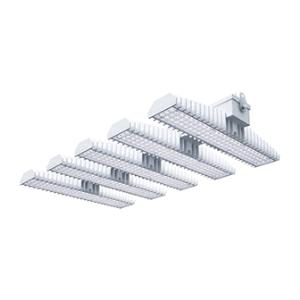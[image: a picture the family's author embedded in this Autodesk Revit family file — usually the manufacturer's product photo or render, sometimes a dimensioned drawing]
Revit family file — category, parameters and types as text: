
# Revit family: 3f_filippi_-_3f_lem_ho_ampio_3f_filippi_-_58976_a0811_-_3f_lem_5_ho_led_350_dali_cr_ampio___vt_9d90
name_source: partatom
category: Lighting Fixtures
units: mm (PartAtom-declared; Revit-internal decimal feet)

## family parameters
Cut with Voids When Loaded = No
Host = Face
Light Source = No
Part Type = Normal
Room Calculation Point = No
Round Connector Dimension = Use Diameter
Shared = No

## types (1)
- 3F Filippi - 3F LEM HO Ampio (1 x LED, 52628 lm, 345 W, 4000 K)
    Apparent Load = 345 VA
    Approval mark = CE
    CIE Flux Codes = 60 92 99 100 100
    Color Rendering = 80
    Color Temperature = 4000 K
    Control Gear = Electronic transformer
    Default Elevation = 1800 mm
    Description = Industrial luminaire with high light output and high luminous efficiency designed with the most innovative technologies for environments with temperature up to 55°C.

ILLUMINOTECHNICAL
Luminous efficiency 100% (DLOR 99%, ULOR 1%).
Initial luminous flux of the luminaire 52628 lm.
Direct symmetric wide distribution: the illuminated area has a rectangular shape.
Installation Interdistance Transv.D = 1.58 x hu - Long.D = 1.45 x hu.
Tabular UGR (CIE 117 - 4H-8H; S=0.25H; 70/50/20): RUG 23.9 - 24.9.
Beam angle: 93° - 99°.
Luminous efficacy 153 lm/W.
Lifetime (L93/B10): 30000 h. (tq+25°C)
Lifetime (L90/B10): 50000 h. (tq+25°C)
Lifetime (L85/B10): 80000 h. (tq+25°C)
Lifetime (L80/B10): 100000 h. (tq+25°C)
Lifetime (L85/B10): 50000 h. (tq+55°C)
Sudden decreased luminous flux after 50000 hours: 0% (C0).
Photobiological safety in compliance with IEC/TR 62778: RG0 risk exempt, (IEC 62471).
In compliance with IEC/EN 62722-2-1 - IEC/EN 62717 standards.

SOURCE
5 Mid-Power linear LED modules 70W/840.
Energy efficiency class (UE 2019/2020 - UE 2019/2015): C.
CIE 13.3 Colour rendering index: CRI >80 (R9 <50%).
IES TM-30 Fidelity Index: Rf = 84 Rg = 95.
CCT nominal colour temperature 4000 K.
Colour initial tolerance (MacAdam): SDCM 3.

MECHANICAL
Passive modular heatsinks in die-casted aluminium, painted in white colour.
To optimize the thermal management of the LED module, the heatsinks are oversized and provided with self-cleaning of cooling fins.
Wiring body in aluminium and galvanised steel anchored solidly to the sinks and thermally separated.
3F Lens lenses with high luminous efficiency, transparent methacrylate (PMMA), fixed to the LED modules.
Fixing brackets in stainless steel.
Luminaire with limited surface temperature. - D - (EN 60598-2-24)
Dimensions: 952x542 mm, height 133 mm. Weight 24.19 kg.
IP65 protection degree.
Mechanical strength to impacts IK06 (1 joule).
Glow-wire test resistance 650°C.

ELECTRICAL
Halogen Free DALI-2 DATI (Parts 251, 252, 253), PUSH-DIM, electronic wiring 230V-50/60Hz, power factor 0.97 at full load, THD <25%, constant output current, class I, 3 driver, 3 DALI addresses.
Power of the luminaire 345 W.
ENEC - CE.
SAFE FLICKER: PstLM=<1 and SVM=<0.4 (IEC TR 61547-1 and IEC TR 63158), to ensure a more comfortable and safe light.
Luminaire compliant with EN 60598-2-22 for power supply from a centralised emergency system CPSS (Central Power Supply System), not incorporated in the luminaire - high risk areas excluded. The default power and flux are 100% in AC and 15% in DC.
Ambient temperature from -30°C to +55°C.
Temperature class T6 max 85°C.
Quick connection via M25 5P connector with 9-13 mm tightening range.
Power unit positioned on a separate compartment by the LED module to ensure optimum temperatures of cabling components, to be inspectable and maintainable.
Relative humidity UR: <85%.

INSTALLATION
Ceiling / Suspended / Wall.
All accessories dedicated to this product are available on the Catalog and on our website www.3F-Filippi.com.

ACCESSORIES
A0811 - VT transparent glass, tempered, not flammable, with sealing gasket.
One required for each light module. The pack contains 10 pieces.

APPLICATIONS
In commercial environments, exhibition and industrial areas, stores, open areas.
Environments in which it is necessary a total protection against falling fragments (eg environments with foodstuffs or machines with moving parts or with extreme temperature changes), use luminaires with polycarbonate lenses.

LIGHT MANAGEMENT
Recommended minimum setting: 10%.
The luminaire, equipped with (DALI-2 DATI) driver, can be controlled manually with 3F Easy Dim technology or automatically/manually with wired or wireless DALI/D2D control systems.
The D2D driver guarantees interoperability with other devices with the same certification by making the following information available:
Device Data (Part 251), Energy Report (Part 252), Diagnosis & Maintenance (Part 253).
In electrical systems without a regulation system (manual or automatic) and DALI bus, a suitable jumper must be made on the DA-DA terminals of the appliance.

WARNING
Fixture not suitable for cold stores with an ambient temperature <0°C and/or relative humidity >85%.
Luminaire designed for disposal/recycling at end-of-life.
Replaceable (LED only) light source by a professional. Replaceable control gear by a professional.
    Height = 133 mm  [stored 0.436352 ft]
    Lamp = 1 x LED
    Lamp Light Flux = 52628 lm
    Lamp Power = 345 W
    Lamp count = 1
    Length = 952 mm
    Lifetime = 50000 h
    Luminous efficacy = 153 lm/W
    Manufacturer = 3F Filippi
    ModVariant = No
    Model = 3F Filippi - 58976+A0811 - 3F LEM 5 HO LED 350 DALI CR AMPIO + VT
    Mounting Place = Ceiling
    Mounting Type = Pendant
    Number of Poles = 1
    OnlyDefault = Yes
    Power Factor = 1
    Product Name = 3F Filippi - 3F LEM HO Ampio
    Product group = pendant luminaire
    ProductGroupID = 9
    Protection Class = Protection class I
    Protection Degree = IP 65
    RLX_Detail_Level = 1
    RLX_Emergency_Light_Flux = 0 lm
    RLX_Emergency_Type = 0
    RLX_Emergency_Type_DB = No
    RlxData = <blob elided: 129273 chars, md5=6aa2a588>
    Socket = socket
    Standby Power = 0 W
    System Light Flux = 52628 lm
    System Power = 345 W
    Type Comments = Product without accessories
    Type Image = 3f_filippi_-_lem_5__a0811.jpg
    URL = http://relux.com
    VarID = ---
    Voltage = 0 V
    Weight = 0.00 kg
    Width = 542 mm

note: [stored X ft] marks values corroborated as IEEE doubles in the binary element streams (Revit-internal decimal feet)

## geometry (parser evidence)
native form markers: Blend x4, Sweep x11
no freeform markers — native parametric forms only
